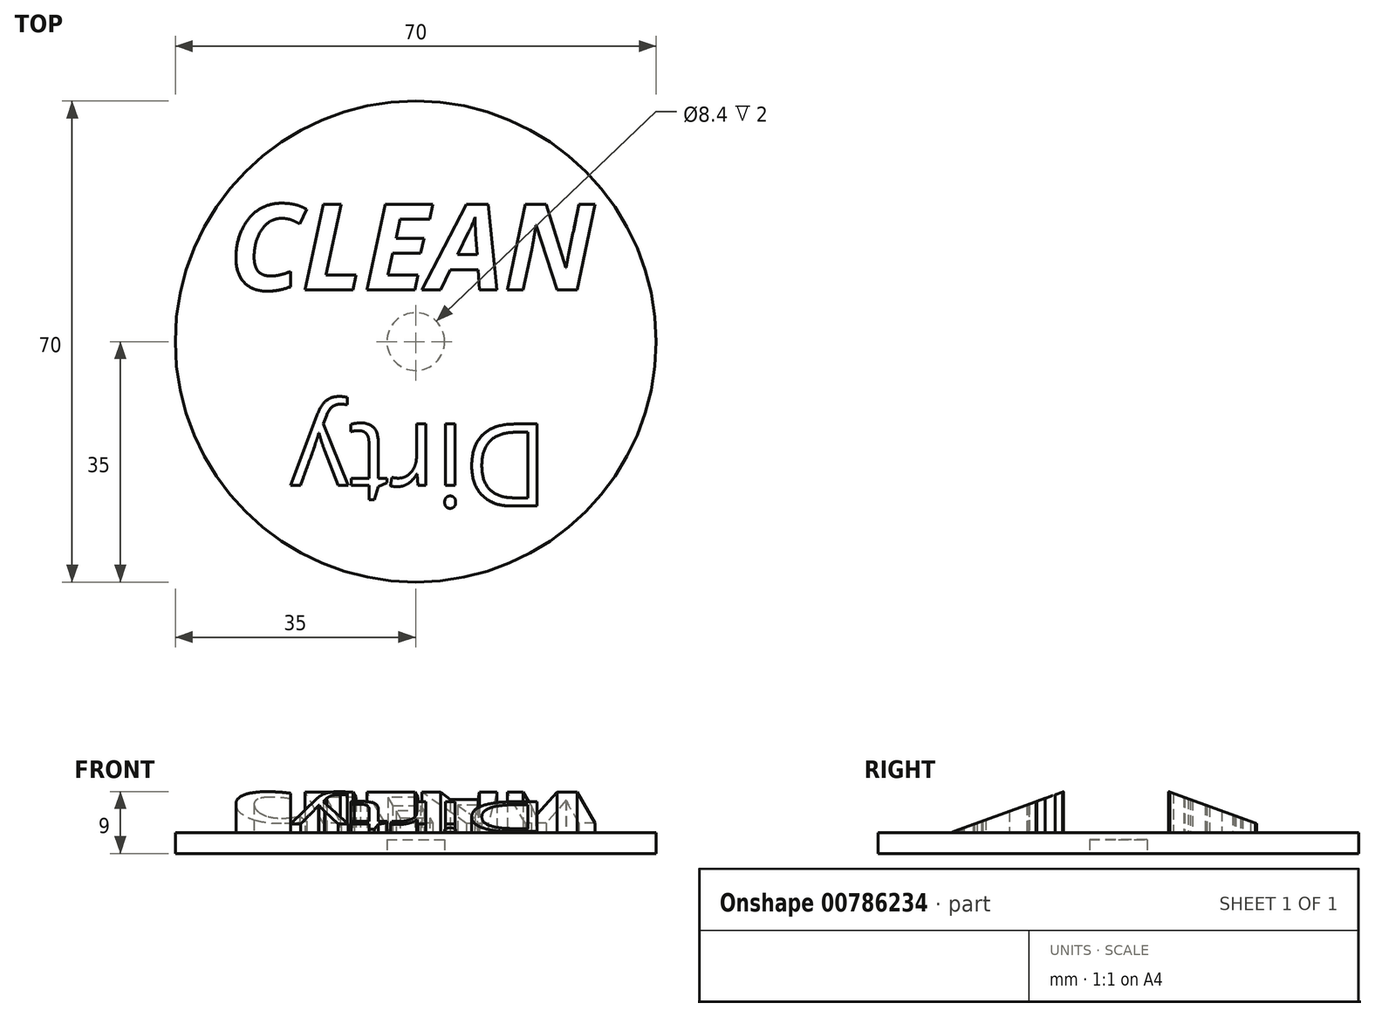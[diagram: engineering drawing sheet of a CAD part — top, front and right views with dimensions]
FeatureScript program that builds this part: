
annotation { "Feature Type Name" : "Feature", "Feature Type Description" : "" }
export const myFeature = defineFeature(function(context is Context, id is Id, definition is map)
    precondition{}
    {
        {
            var Q0;
            Q0=qCreatedBy(makeId("Top.planeOp"),FACE);
            var sketch = newSketch(context, id + "F0", { "sketchPlane" : qUnion([Q0])});
            skCircle(sketch, "E0", {"center": v(0, 0) * mm, "radius": 35 * mm});
            skSolve(sketch);
        }
        {
            var Q0;
            Q0=makeQuery(id+"F0.imprint","IMPRINT",FACE,{"disambiguationData":[TD([[makeQuery(id+"F0.imprint","IMPRINT",EDGE,{"derivedFrom":sQuery(id+"F0.wireOp",EDGE,"E0")}),1.0]])]});
            extrude(context, id + "F1", {"entities" : qUnion([Q0]), "depth" : 3 * mm, "offsetDistance" : 25 * mm});
        }
        {
            var Q0;
            Q0=makeQuery(id+"F1.opExtrude","CAP_FACE",FACE,{"disambiguationData":[OSD([sQuery(id+"F0.wireOp",EDGE,"E0")])],"isStart":false});
            var sketch = newSketch(context, id + "F2", { "sketchPlane" : qUnion([Q0])});
            skText(sketch, "E1", { "text": "CLEAN", "fontName": "OpenSans-BoldItalic.ttf"});
            skText(sketch, "E2", { "text": "Dirty", "fontName": "OpenSans-Regular.ttf"});
            skLineSegment(sketch, "E3", {"start": v(0, -12) * mm, "end": v(0, 0) * mm});
            const initialGuessF2  = {"E1": [-0.02722, 0.0075, 1, 0, 0.01255], "E2": [0.01933, -0.012, -1, 0, 0.01204]};
            skSetInitialGuess(sketch, initialGuessF2);
            skSolve(sketch);
        }
        {
            var Q0;
            Q0 = qSketchRegion(id + "F2", true);
            extrude(context, id + "F3", {"entities" : qUnion([Q0]), "depth" : 6 * mm, "offsetDistance" : 25 * mm});
        }
        {
            var Q0;
            Q0=qCreatedBy(makeId("Right.planeOp"),FACE);
            var sketch = newSketch(context, id + "F4", { "sketchPlane" : qUnion([Q0])});
            skLineSegment(sketch, "E4.0", {"start": v(7.33, 9) * mm, "end": v(7.33, 3) * mm});
            skLineSegment(sketch, "E5", {"start": v(7.33, 9) * mm, "end": v(20.26, 4.3) * mm});
            skLineSegment(sketch, "E6", {"start": v(20.26, 4.3) * mm, "end": v(20.26, 9) * mm});
            skLineSegment(sketch, "E7", {"start": v(7.33, 9) * mm, "end": v(20.26, 9) * mm});
            skFitSpline(sketch, "E8.0", {"points": [v(-8.61, 11) * mm, v(-8.4, 11) * mm, v(-8.2, 11) * mm, v(-7.98, 11) * mm]});
            skLineSegment(sketch, "E9", {"start": v(-7.98, 9) * mm, "end": v(-24.32, 9) * mm});
            skLineSegment(sketch, "E10", {"start": v(-24.32, 9) * mm, "end": v(-24.32, 3.05) * mm});
            skLineSegment(sketch, "E11", {"start": v(-24.32, 3.05) * mm, "end": v(-7.98, 9) * mm});
            skSolve(sketch);
        }
        {
            var Q0;
            Q0 = qSketchRegion(id + "F4", true);
            extrude(context, id + "F5", {"entities" : qUnion([Q0]), "operationType" : NewBodyOperationType.REMOVE, "endBound" : BoundingType.THROUGH_ALL, "oppositeDirection" : true, "depth" : 25 * mm, "offsetDistance" : 25 * mm, "hasSecondDirection" : true, "secondDirectionBound" : SecondDirectionBoundingType.THROUGH_ALL, "secondDirectionOppositeDirection" : false, "secondDirectionDepth" : 25 * mm});
        }
        {
            var Q0;
            Q0=makeQuery(id+"F1.opExtrude","CAP_FACE",FACE,{"disambiguationData":[OSD([sQuery(id+"F0.wireOp",EDGE,"E0")])],"isStart":true});
            var sketch = newSketch(context, id + "F6", { "sketchPlane" : qUnion([Q0])});
            skCircle(sketch, "E12", {"center": v(0, 0) * mm, "radius": 4.2 * mm});
            skSolve(sketch);
        }
        {
            var Q0;
            Q0 = qSketchRegion(id + "F6", true);
            extrude(context, id + "F7", {"entities" : qUnion([Q0]), "operationType" : NewBodyOperationType.REMOVE, "oppositeDirection" : true, "depth" : 2 * mm, "offsetDistance" : 25 * mm});
        }
    });
